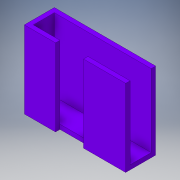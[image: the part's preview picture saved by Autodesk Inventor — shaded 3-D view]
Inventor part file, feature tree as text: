
AUTODESK INVENTOR PART (.ipt)
format: ipt  version: 2019 (Build 230136000, 136)  size: 131,072 bytes
history: native  units: mm
features: extrude x2, sketch x2, projected_geometry x1
ambient origin geometry x8: Origin, YZ Plane, XZ Plane, XY Plane, X Axis, Y Axis, Z Axis, Center Point
bodies: Solid1 (feature_tree)
feature tree (5):
  extrude  "Extrusion1"  Depth=15.0mm
  extrude  "Extrusion2"  Depth=72.18mm
  sketch  "Sketch1"  dims[d0=69.0mm d1=15.0mm]
  sketch  "Sketch2"  dims[d2=3.18mm d3=0.0mm d4=72.18mm d5=3.18mm d6=30.0mm d7=3.18mm d8=20.0mm d9=22.18mm d10=55.0mm d11=0.0mm]
  projected_geometry  "Projected Loop1"
